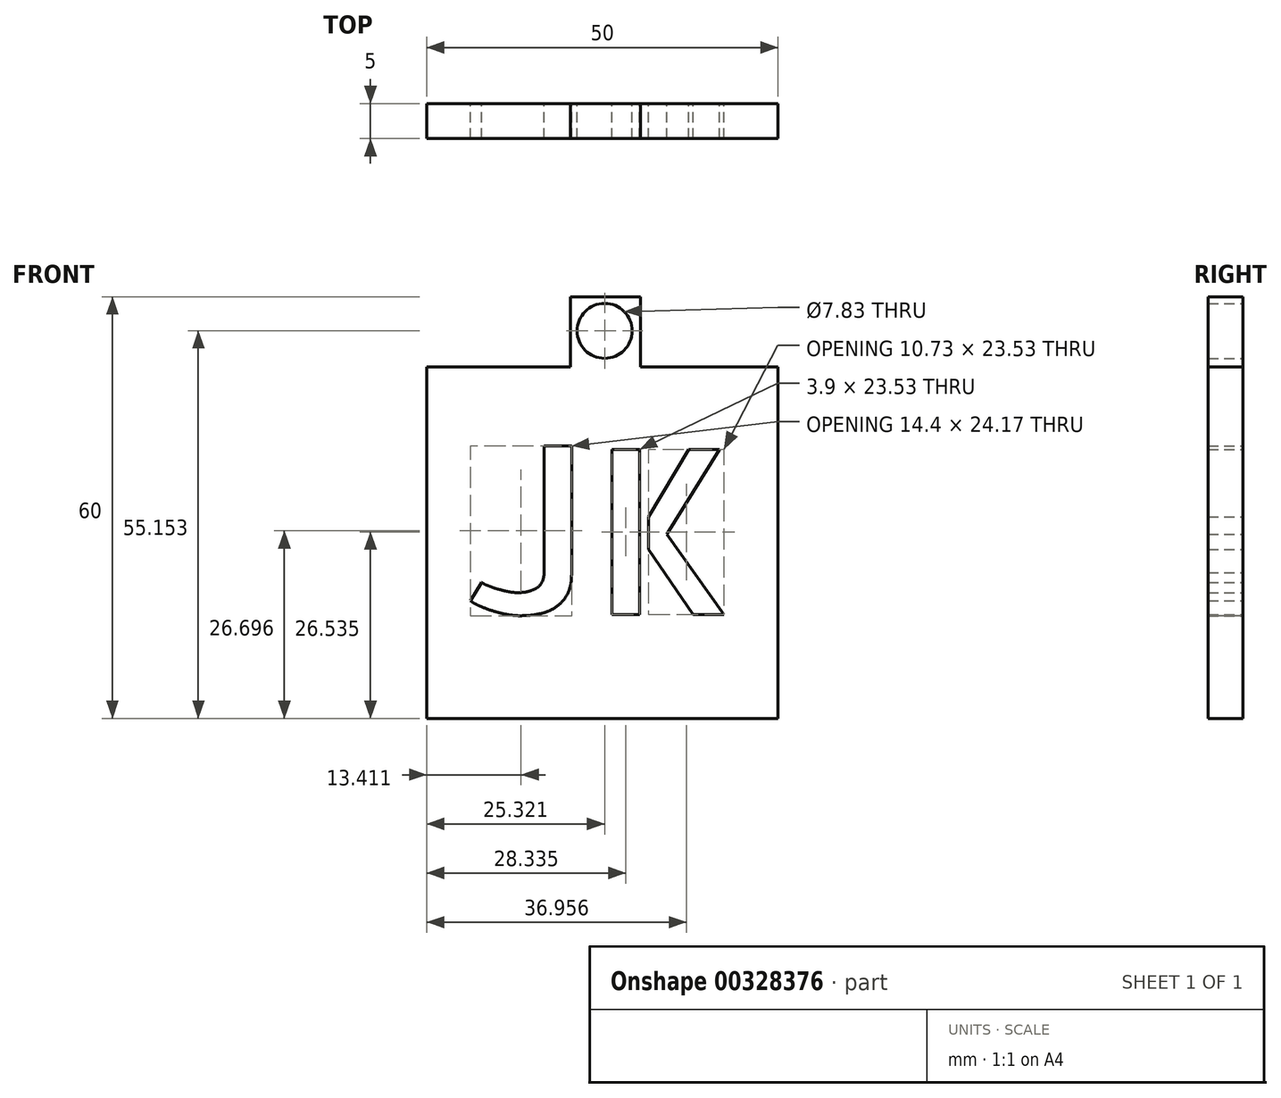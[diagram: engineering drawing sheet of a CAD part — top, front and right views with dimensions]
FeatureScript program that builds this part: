
annotation { "Feature Type Name" : "Feature", "Feature Type Description" : "" }
export const myFeature = defineFeature(function(context is Context, id is Id, definition is map)
    precondition{}
    {
        {
            var Q0;
            Q0=qCreatedBy(makeId("Front.planeOp"),FACE);
            var sketch = newSketch(context, id + "F0", { "sketchPlane" : qUnion([Q0])});
            skLineSegment(sketch, "E0.bottom", {"start": v(-24.3, 0) * mm, "end": v(25.7, 0) * mm});
            skLineSegment(sketch, "E0.left", {"start": v(-24.3, 0) * mm, "end": v(-24.3, 50) * mm});
            skLineSegment(sketch, "E0.right", {"start": v(25.7, 0) * mm, "end": v(25.7, 50) * mm});
            skLineSegment(sketch, "E1.top", {"start": v(-3.87, 60) * mm, "end": v(6.13, 60) * mm});
            skLineSegment(sketch, "E1.left", {"start": v(-3.87, 50) * mm, "end": v(-3.87, 60) * mm});
            skLineSegment(sketch, "E1.right", {"start": v(6.13, 50) * mm, "end": v(6.13, 60) * mm});
            skCircle(sketch, "E2", {"center": v(1.02, 55.15) * mm, "radius": 3.91 * mm});
            skLineSegment(sketch, "E3", {"start": v(-24.3, 50) * mm, "end": v(-3.87, 50) * mm});
            skLineSegment(sketch, "E4", {"start": v(6.13, 50) * mm, "end": v(25.7, 50) * mm});
            skSolve(sketch);
        }
        {
            var Q0;
            Q0=makeQuery(id+"F0.imprint","IMPRINT",FACE,{"disambiguationData":[TD([[makeQuery(id+"F0.imprint","IMPRINT",EDGE,{"derivedFrom":sQuery(id+"F0.wireOp",EDGE,"E0.bottom")}),1.0]])]});
            var sketch = newSketch(context, id + "F1", { "sketchPlane" : qUnion([Q0])});
            skText(sketch, "E5", { "text": "JK", "fontName": "AllertaStencil-Regular.ttf"});
            const initialGuessF1  = {"E5": [-0.01892, 0.01477, 1, 0, 0.02354]};
            skSetInitialGuess(sketch, initialGuessF1);
            skSolve(sketch);
        }
        {
            var Q0;
            Q0=makeQuery(id+"F1.imprint","IMPRINT",FACE,{"disambiguationData":[TD([[makeQuery(id+"F1.imprint","IMPRINT",EDGE,{"derivedFrom":sQuery(id+"F1.wireOp",EDGE,"E5.sketch_text.stroke-0")}),1.0]])]});
            extrude(context, id + "F2", {"entities" : qUnion([Q0]), "depth" : 5 * mm});
        }
    });
